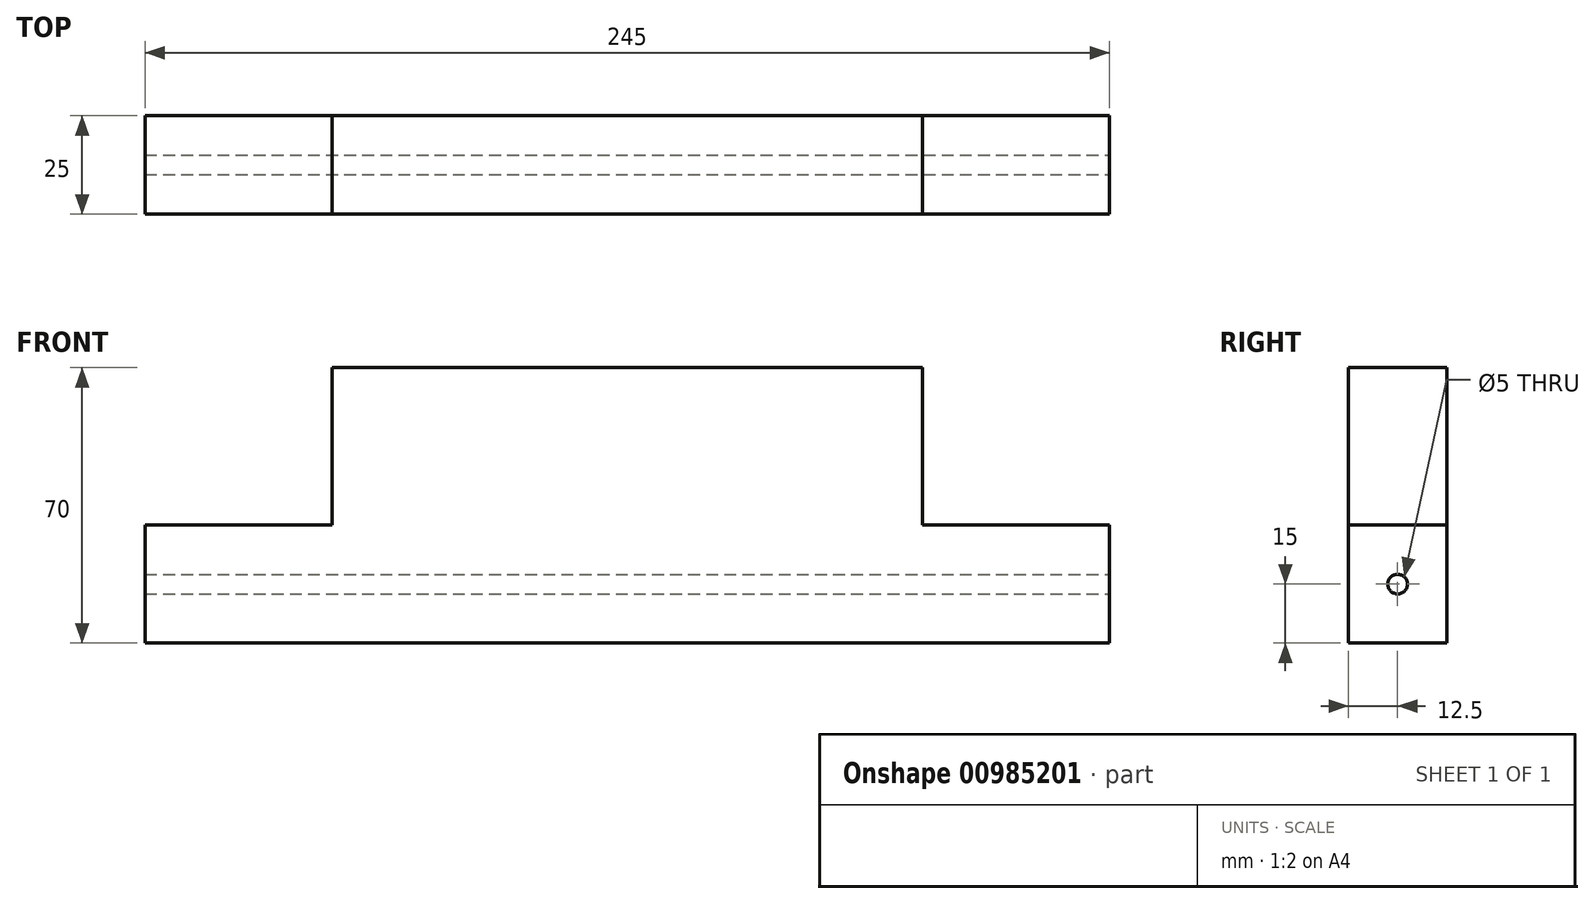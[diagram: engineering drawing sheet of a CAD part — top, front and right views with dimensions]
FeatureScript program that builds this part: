
annotation { "Feature Type Name" : "Feature", "Feature Type Description" : "" }
export const myFeature = defineFeature(function(context is Context, id is Id, definition is map)
    precondition{}
    {
        {
            var Q0;
            Q0=qCreatedBy(makeId("Front.planeOp"),FACE);
            var sketch = newSketch(context, id + "F0", { "sketchPlane" : qUnion([Q0])});
            skLineSegment(sketch, "E0", {"start": v(-122.5, 0) * mm, "end": v(-122.5, 30) * mm});
            skLineSegment(sketch, "E1", {"start": v(-122.5, 30) * mm, "end": v(-75, 30) * mm});
            skLineSegment(sketch, "E2", {"start": v(-75, 30) * mm, "end": v(-75, 70) * mm});
            skLineSegment(sketch, "E3", {"start": v(-75, 70) * mm, "end": v(0, 70) * mm});
            skLineSegment(sketch, "E4", {"start": v(0, 70) * mm, "end": v(0, 0) * mm});
            skLineSegment(sketch, "E5", {"start": v(0, 0) * mm, "end": v(-122.5, 0) * mm});
            skLineSegment(sketch, "E6.MirrorCS", {"start": v(122.5, 30) * mm, "end": v(75, 30) * mm});
            skLineSegment(sketch, "E7.MirrorCS", {"start": v(122.5, 0) * mm, "end": v(122.5, 30) * mm});
            skLineSegment(sketch, "E8.MirrorCS", {"start": v(0, 0) * mm, "end": v(122.5, 0) * mm});
            skLineSegment(sketch, "E9.MirrorCS", {"start": v(75, 30) * mm, "end": v(75, 70) * mm});
            skLineSegment(sketch, "E10.MirrorCS", {"start": v(75, 70) * mm, "end": v(0, 70) * mm});
            skSolve(sketch);
        }
        {
            var Q0;
            Q0 = qSketchRegion(id + "F0", true);
            extrude(context, id + "F1", {"entities" : qUnion([Q0]), "depth" : 25 * mm, "offsetDistance" : 25 * mm});
        }
        {
            var Q0;
            Q0=makeQuery(id+"F1.opExtrude","SWEPT_FACE",FACE,{"disambiguationData":[OSD([sQuery(id+"F0.wireOp",EDGE,"E7.MirrorCS")])]});
            var sketch = newSketch(context, id + "F2", { "sketchPlane" : qUnion([Q0])});
            skPoint(sketch, "E11", {"position": v(-12.5, 15) * mm});
            skSolve(sketch);
        }
        {
            var Q0;
            Q0=sQuery(id+"F2.wireOp",VERTEX,"E11");
            var Q1;
            Q1=makeQuery(id+"F1.opExtrude","SWEPT_BODY",BODY,{"disambiguationData":[OSD([sQuery(id+"F0.wireOp",EDGE,"E0"),sQuery(id+"F0.wireOp",EDGE,"E1"),sQuery(id+"F0.wireOp",EDGE,"E2"),sQuery(id+"F0.wireOp",EDGE,"E3"),sQuery(id+"F0.wireOp",EDGE,"E5"),sQuery(id+"F0.wireOp",EDGE,"E6.MirrorCS"),sQuery(id+"F0.wireOp",EDGE,"E7.MirrorCS"),sQuery(id+"F0.wireOp",EDGE,"E8.MirrorCS"),sQuery(id+"F0.wireOp",EDGE,"E9.MirrorCS"),sQuery(id+"F0.wireOp",EDGE,"E10.MirrorCS")])]});
            hole(context, id + "F3", {"style" : HoleStyle.SIMPLE, "endStyle" : HoleEndStyle.THROUGH, "holeDiameter" : 5 * mm, "majorDiameter" : 5 * mm, "isTappedThrough" : true, "tappedDepth" : 12 * mm, "tapClearance" : 3, "locations" : qUnion([Q0]), "scope" : qUnion([Q1])});
        }
    });
